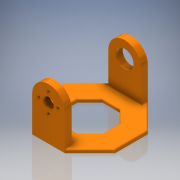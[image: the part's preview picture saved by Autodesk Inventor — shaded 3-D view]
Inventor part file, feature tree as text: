
AUTODESK INVENTOR PART (.ipt)
format: ipt  version: 2017 (Build 210142000, 142)  size: 257,536 bytes
history: native  units: mm
features: extrude x6, sketch x6, fillet x3, chamfer x1
ambient origin geometry x8: Origin, YZ Plane, XZ Plane, XY Plane, X Axis, Y Axis, Z Axis, Center Point
bodies: Solid1 (feature_tree)
feature tree (16):
  extrude  "Extrusion1"  Depth=61.0mm
  extrude  "Extrusion2"  TaperAngle=0.0deg  [1 undecoded]
  chamfer  "Chamfer1"  Distance=18.5mm
  fillet  "Fillet3"  Radius=2.0mm
  fillet  "Fillet4"  Radius=10.0mm
  extrude  "Extrusion3"  Depth=10.0mm
  extrude  "Extrusion4"  Depth=10.0mm
  extrude  "Extrusion5"  Depth=10.0mm
  fillet  "Fillet5"  Radius=7.0mm
  extrude  "Extrusion6"  Depth=10.0mm
  sketch  "Sketch1"  dims[d0=61.0mm d1=61.0mm]
  sketch  "Sketch2"  dims[d2=2.5mm d3=0.0mm]
  sketch  "Sketch3"  dims[d4=5.0mm]
  sketch  "Sketch4"  dims[d5=35.5mm]
  sketch  "Sketch5"  dims[d6=0.0mm]
  sketch  "Sketch6"  dims[d7=24.0mm d8=18.5mm d9=2.0mm d10=45.0deg d11=10.0mm d12=0.0mm d13=2.0mm d14=7.0mm d15=7.0mm d16=7.0mm d17=7.0mm d18=13.0mm d19=10.0mm d20=0.0mm d21=15.0mm d22=10.0mm d23=0.0mm d24=1.0mm d25=7.7mm d26=10.0mm d27=0.0mm]
note: 1 required parameter value undecoded (feature->parameter linkage not recoverable at this tier; creation-order binding heuristic only, values carry confidence <= 0.55)
